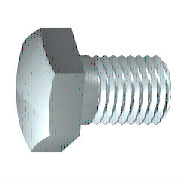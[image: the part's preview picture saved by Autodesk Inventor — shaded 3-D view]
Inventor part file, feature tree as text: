
AUTODESK INVENTOR PART (.ipt)
format: ipt  version: 2023.2 (Build 272271030, 271C)  size: 190,464 bytes
history: native  units: mm (DEFAULTED — no unit token found)
features: sketch x3, extrude x1, chamfer x1, plane x1
ambient origin geometry x7: Origin, YZ Plane, XZ Plane, X Axis, Y Axis, Z Axis, Center Point
bodies: Solid1 (feature_tree), Body (feature_tree)
feature tree (6):
  extrude  "Head"  Depth=94.0mm
  chamfer  "Chamfer1"  Distance=8.2mm
  plane  "Work Plane1"
  sketch  "Sketch1"  dims[d0=100.0mm d1=94.0mm]
  sketch  "Sketch2"  dims[d2=14.0mm]
  sketch  "Sketch4"  dims[d12=90.0deg d3=8.2mm d4=0.0mm d5=30.0deg d21=90.0deg d6=1.2269mm d7=1.227mm d8=0.0mm d9=0.6001mm d10=19.64mm d11=21.0mm d13=1.227mm d14=14.0mm d15=94.0mm d16=0.0mm d19=21.0mm d55=45.0deg d57=0.0mm d58=0.0mm]
